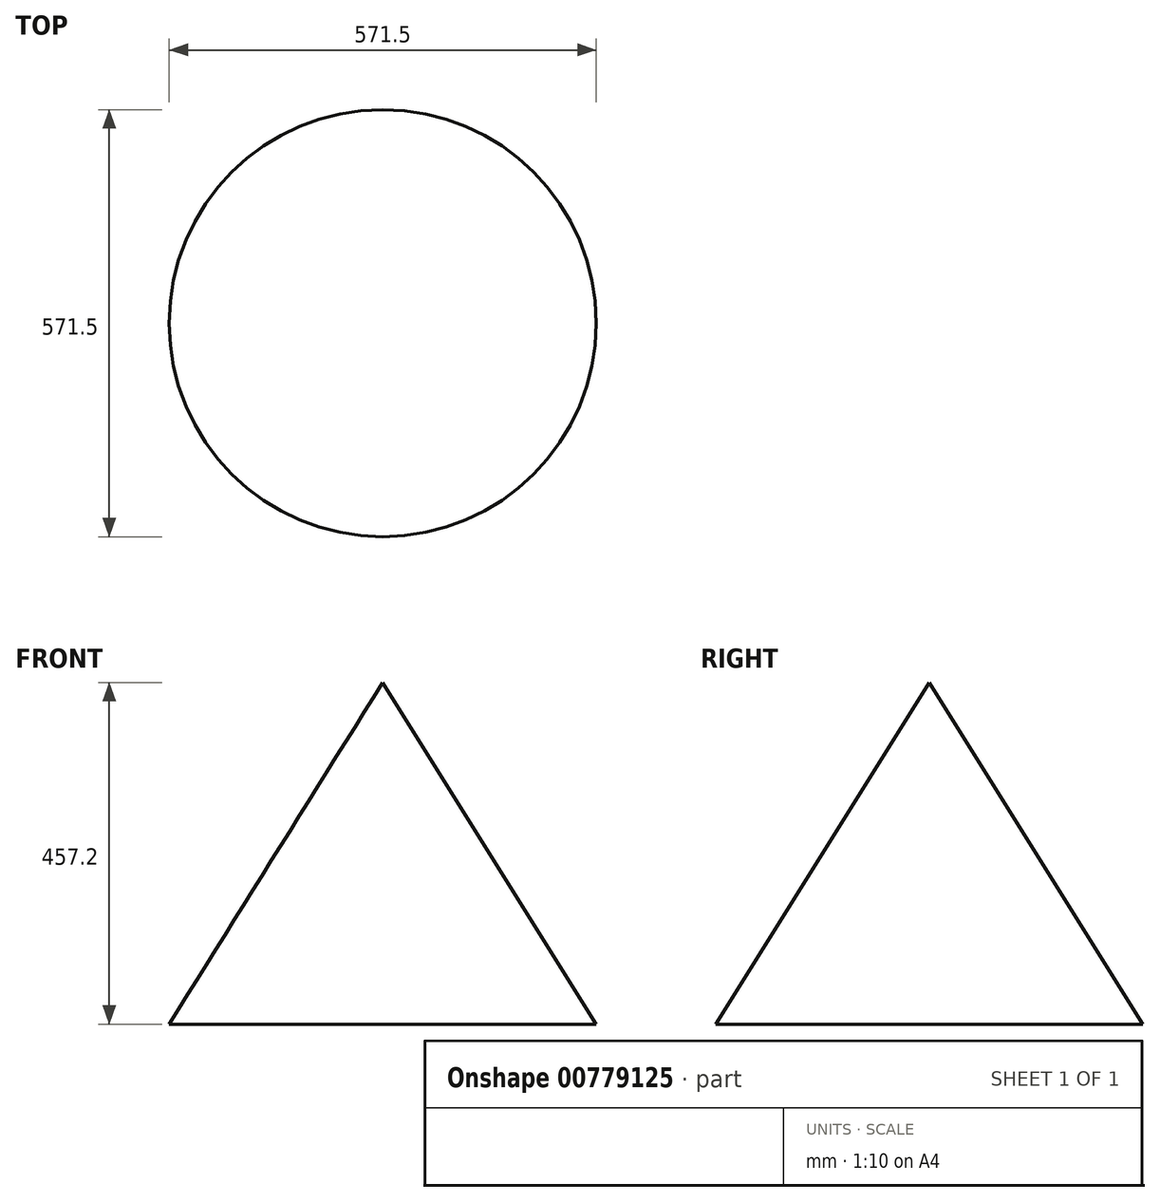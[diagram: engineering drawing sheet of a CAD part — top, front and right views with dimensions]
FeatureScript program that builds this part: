
annotation { "Feature Type Name" : "Feature", "Feature Type Description" : "" }
export const myFeature = defineFeature(function(context is Context, id is Id, definition is map)
    precondition{}
    {
        {
            var Q0;
            Q0=qCreatedBy(makeId("Front.planeOp"),FACE);
            var sketch = newSketch(context, id + "F0", { "sketchPlane" : qUnion([Q0])});
            skLineSegment(sketch, "E0", {"start": v(0, 0) * mm, "end": v(-285.75, 0) * mm});
            skLineSegment(sketch, "E1", {"start": v(0, 0) * mm, "end": v(0, 457.2) * mm});
            skLineSegment(sketch, "E2", {"start": v(-285.75, 0) * mm, "end": v(0, 457.2) * mm});
            skSolve(sketch);
        }
        {
            var Q0;
            Q0 = qSketchRegion(id + "F0", true);
            var Q1;
            Q1=sQuery(id+"F0.wireOp",EDGE,"E1");
            revolve(context, id + "F1", {"surfaceOperationType" : NewSurfaceOperationType.NEW, "entities" : qUnion([Q0]), "axis" : qUnion([Q1]), "revolveType" : RevolveType.FULL});
        }
    });
